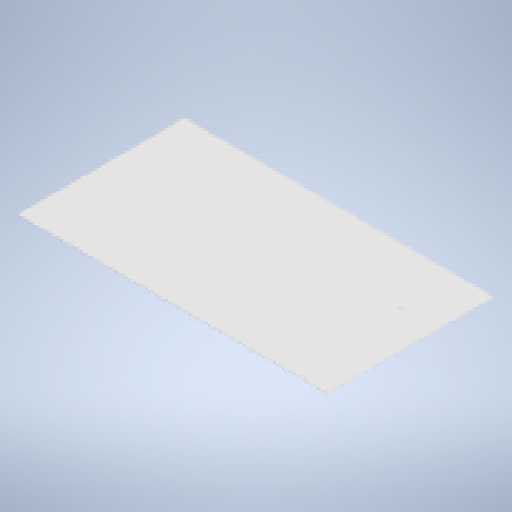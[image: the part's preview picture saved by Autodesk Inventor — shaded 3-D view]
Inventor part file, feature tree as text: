
AUTODESK INVENTOR PART (.ipt)
format: ipt  version: 2025 (Build 290162010, 162A)  size: 235,008 bytes
history: native  units: mm
features: other x3, sketch x3, sheet_metal_op x1, extrude x1
ambient origin geometry x8: Origin, YZ Plane, XZ Plane, XY Plane, X Axis, Y Axis, Z Axis, Center Point
bodies: Solid1 (feature_tree)
feature tree (8):
  sheet_metal_op  "Face1"
  other  "Mark1"
  extrude  "Extrusion2"  Depth=1480.0mm
  sketch  "Sketch1"  dims[d0=2748.0mm d1=1480.0mm]
  other  "Plate1"
  sketch  "Sketch5"  dims[d2=3.0mm]
  sketch  "Sketch6"  dims[d26=200.0mm d27=15.0mm d28=25.0mm d29=25.0mm d30=40.0mm d31=400.0mm d32=320.0mm d33=10.0mm d34=0.0mm]
  other  "Definition1"
